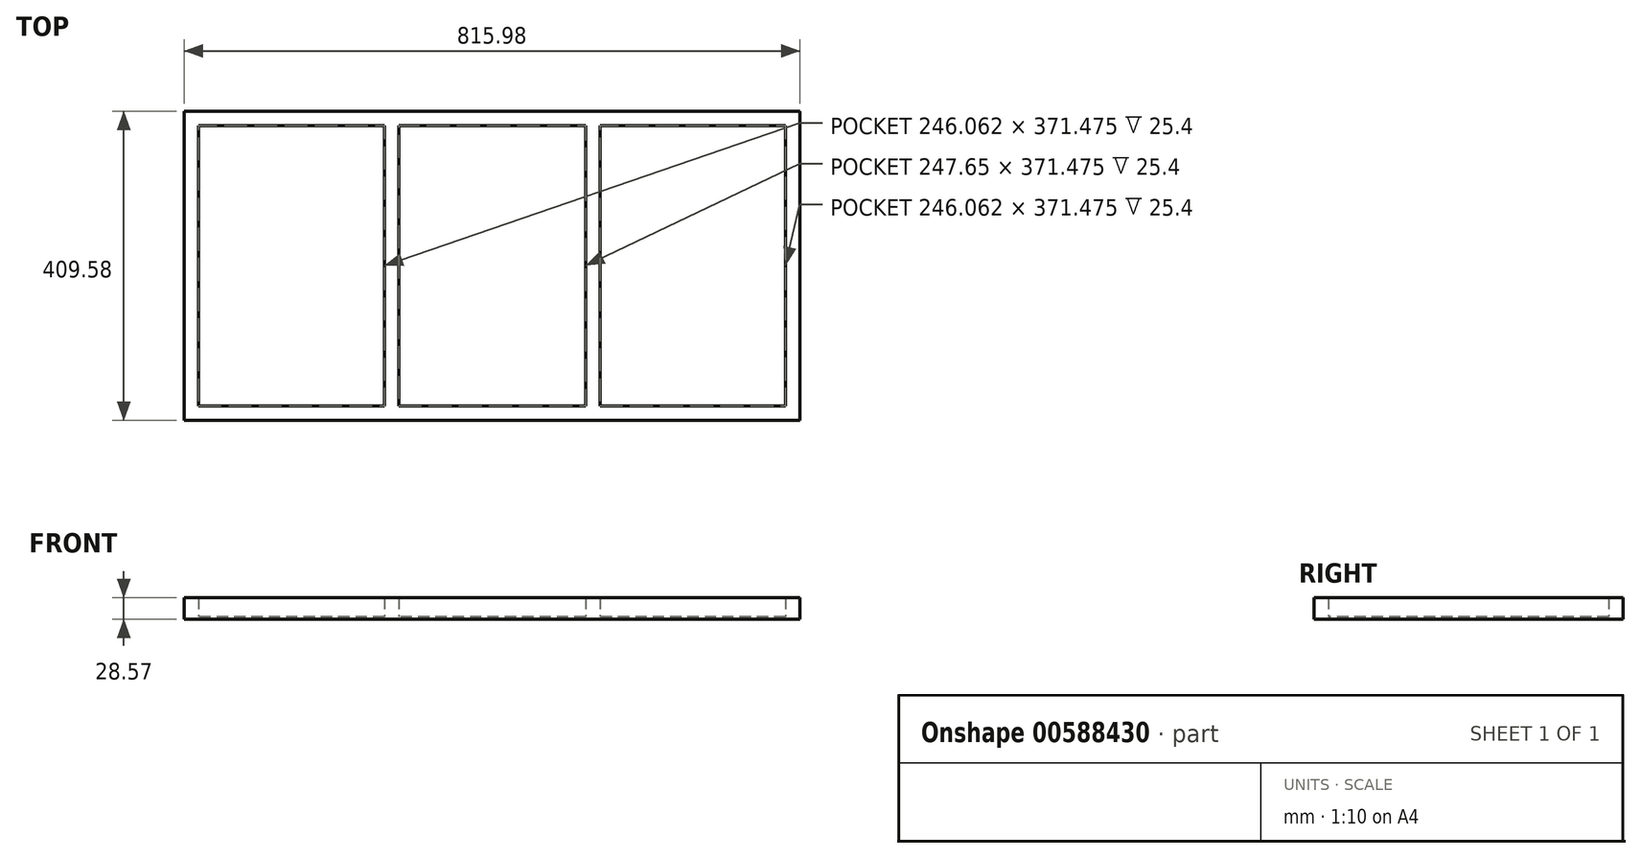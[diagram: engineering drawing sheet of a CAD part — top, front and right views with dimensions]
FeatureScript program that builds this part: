
annotation { "Feature Type Name" : "Feature", "Feature Type Description" : "" }
export const myFeature = defineFeature(function(context is Context, id is Id, definition is map)
    precondition{}
    {
        {
            var Q0;
            Q0=qCreatedBy(makeId("Top.planeOp"),FACE);
            var sketch = newSketch(context, id + "F0", { "sketchPlane" : qUnion([Q0])});
            skLineSegment(sketch, "E0.bottom", {"start": v(407.99, -204.79) * mm, "end": v(-407.99, -204.79) * mm});
            skLineSegment(sketch, "E0.top", {"start": v(407.99, 204.79) * mm, "end": v(-407.99, 204.79) * mm});
            skLineSegment(sketch, "E0.left", {"start": v(407.99, -204.79) * mm, "end": v(407.99, 204.79) * mm});
            skLineSegment(sketch, "E0.right", {"start": v(-407.99, -204.79) * mm, "end": v(-407.99, 204.79) * mm});
            skPoint(sketch, "E0.middle", {"position": v(0, 0) * mm});
            skSolve(sketch);
        }
        {
            var Q0;
            Q0 = qSketchRegion(id + "F0", true);
            extrude(context, id + "F1", {"entities" : qUnion([Q0]), "depth" : 3.17 * mm, "offsetDistance" : 25.4 * mm});
        }
        {
            var Q0;
            Q0=makeQuery(id+"F1.opExtrude","CAP_FACE",FACE,{"disambiguationData":[OSD([sQuery(id+"F0.wireOp",EDGE,"E0.bottom"),sQuery(id+"F0.wireOp",EDGE,"E0.top"),sQuery(id+"F0.wireOp",EDGE,"E0.left"),sQuery(id+"F0.wireOp",EDGE,"E0.right")])],"isStart":false});
            var sketch = newSketch(context, id + "F2", { "sketchPlane" : qUnion([Q0])});
            skLineSegment(sketch, "E1.0", {"start": v(407.99, -204.79) * mm, "end": v(407.99, 204.79) * mm});
            skLineSegment(sketch, "E1.1", {"start": v(-407.99, -204.79) * mm, "end": v(-407.99, 204.79) * mm});
            skLineSegment(sketch, "E1.2", {"start": v(407.99, -204.79) * mm, "end": v(-407.99, -204.79) * mm});
            skLineSegment(sketch, "E1.3", {"start": v(407.99, 204.79) * mm, "end": v(-407.99, 204.79) * mm});
            skLineSegment(sketch, "E2.0", {"start": v(388.94, 185.74) * mm, "end": v(142.88, 185.74) * mm});
            skLineSegment(sketch, "E2.1", {"start": v(388.94, -185.74) * mm, "end": v(388.94, 185.74) * mm});
            skLineSegment(sketch, "E2.2", {"start": v(388.94, -185.74) * mm, "end": v(142.87, -185.74) * mm});
            skLineSegment(sketch, "E2.3", {"start": v(-388.94, -185.74) * mm, "end": v(-388.94, 185.74) * mm});
            skLineSegment(sketch, "E3", {"start": v(-142.88, 185.74) * mm, "end": v(-142.88, -185.74) * mm});
            skLineSegment(sketch, "E4.0", {"start": v(-123.83, 185.74) * mm, "end": v(-123.83, -185.74) * mm});
            skLineSegment(sketch, "E5.MirrorCS", {"start": v(142.88, 185.74) * mm, "end": v(142.88, -185.74) * mm});
            skLineSegment(sketch, "E6.MirrorCS", {"start": v(123.83, 185.74) * mm, "end": v(123.83, -185.74) * mm});
            skLineSegment(sketch, "E7.trimOffspring", {"start": v(-142.88, 185.74) * mm, "end": v(-388.94, 185.74) * mm});
            skLineSegment(sketch, "E8.trimOffspring", {"start": v(123.83, 185.74) * mm, "end": v(-123.83, 185.74) * mm});
            skLineSegment(sketch, "E9.trimOffspring", {"start": v(123.83, -185.74) * mm, "end": v(-123.83, -185.74) * mm});
            skLineSegment(sketch, "E10.trimOffspring", {"start": v(-142.88, -185.74) * mm, "end": v(-388.94, -185.74) * mm});
            skSolve(sketch);
        }
        {
            var Q0;
            Q0 = qSketchRegion(id + "F2", true);
            extrude(context, id + "F3", {"entities" : qUnion([Q0]), "operationType" : NewBodyOperationType.ADD, "depth" : 25.4 * mm, "offsetDistance" : 25.4 * mm});
        }
    });
